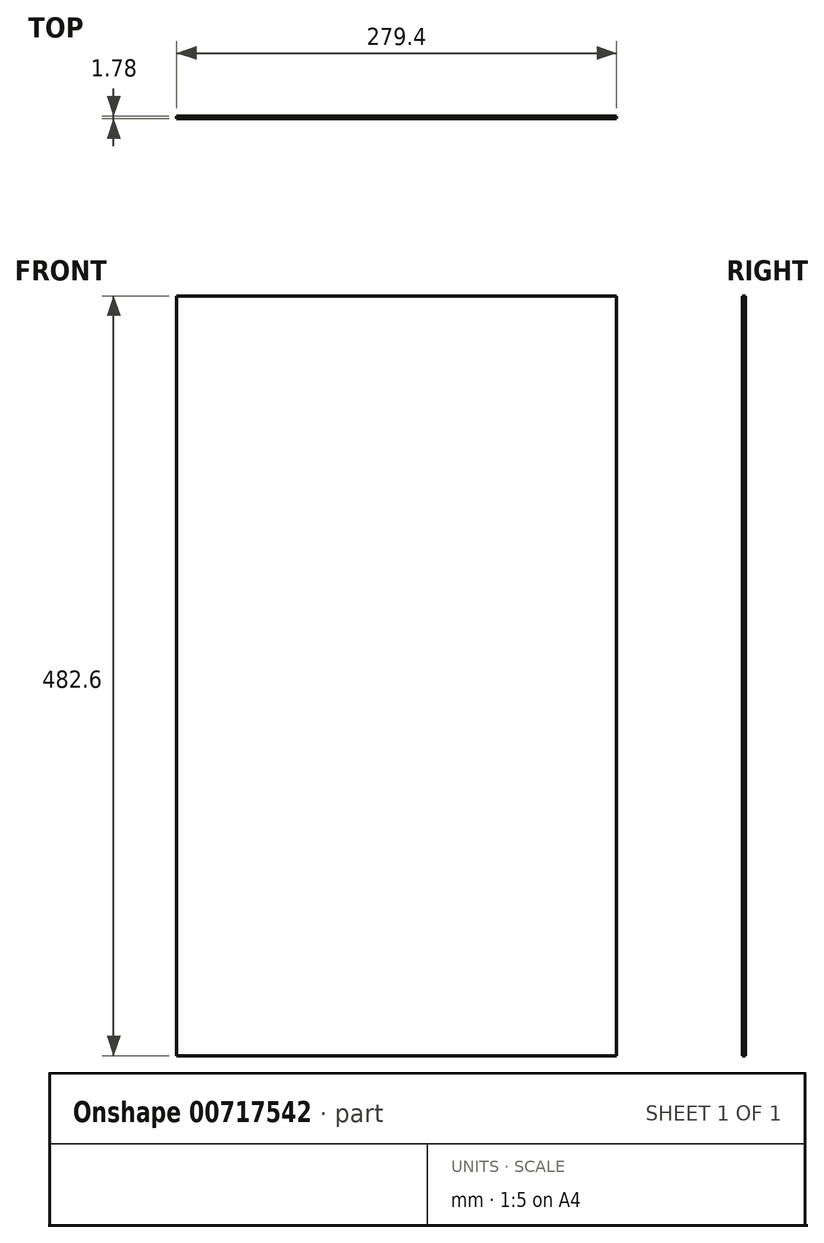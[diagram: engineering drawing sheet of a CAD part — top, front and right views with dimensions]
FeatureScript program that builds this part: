
annotation { "Feature Type Name" : "Feature", "Feature Type Description" : "" }
export const myFeature = defineFeature(function(context is Context, id is Id, definition is map)
    precondition{}
    {
        {
            var Q0;
            Q0=qCreatedBy(makeId("Front.planeOp"),FACE);
            var sketch = newSketch(context, id + "F0", { "sketchPlane" : qUnion([Q0])});
            skLineSegment(sketch, "E0.bottom", {"start": v(-143.3, 241.6) * mm, "end": v(136.1, 241.6) * mm});
            skLineSegment(sketch, "E0.top", {"start": v(-143.3, -241) * mm, "end": v(136.1, -241) * mm});
            skLineSegment(sketch, "E0.left", {"start": v(-143.3, 241.6) * mm, "end": v(-143.3, -241) * mm});
            skLineSegment(sketch, "E0.right", {"start": v(136.1, 241.6) * mm, "end": v(136.1, -241) * mm});
            skLineSegment(sketch, "E1.bottom", {"start": v(0, -241) * mm, "end": v(0, -241) * mm});
            skLineSegment(sketch, "E1.top", {"start": v(0, -281.47) * mm, "end": v(0, -281.47) * mm});
            skLineSegment(sketch, "E1.left", {"start": v(0, -241) * mm, "end": v(0, -281.47) * mm});
            skLineSegment(sketch, "E1.right", {"start": v(0, -241) * mm, "end": v(0, -281.47) * mm});
            skLineSegment(sketch, "E2.bottom", {"start": v(-59.03, -241) * mm, "end": v(-59.03, -241) * mm});
            skLineSegment(sketch, "E2.top", {"start": v(-59.03, -259.98) * mm, "end": v(-59.03, -259.98) * mm});
            skLineSegment(sketch, "E2.left", {"start": v(-59.03, -241) * mm, "end": v(-59.03, -259.98) * mm});
            skLineSegment(sketch, "E2.right", {"start": v(-59.03, -241) * mm, "end": v(-59.03, -259.98) * mm});
            skSolve(sketch);
        }
        {
            var Q0;
            Q0=makeQuery(id+"F0.imprint","IMPRINT",FACE,{"disambiguationData":[TD([[makeQuery(id+"F0.imprint","IMPRINT",EDGE,{"derivedFrom":sQuery(id+"F0.wireOp",EDGE,"E0.bottom")}),-1.0]])]});
            extrude(context, id + "F1", {"entities" : qUnion([Q0]), "depth" : 1.78 * mm, "offsetDistance" : 25.4 * mm});
        }
    });
